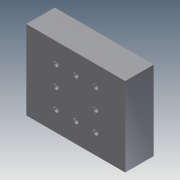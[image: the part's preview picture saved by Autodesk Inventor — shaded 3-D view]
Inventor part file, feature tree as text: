
AUTODESK INVENTOR PART (.ipt)
format: ipt  version: 2011 (Build 150239000, 239)  size: 123,904 bytes
history: native  units: in
note: dims shown in document units (in); Inventor stores cm internally (conversion verified against a paired STEP export)
features: extrude x5, sketch x5
ambient origin geometry x8: Origin, YZ Plane, XZ Plane, XY Plane, X Axis, Y Axis, Z Axis, Center Point
bodies: Solid1 (feature_tree)
feature tree (10):
  extrude  "Extrusion1"  Depth=1.1811in
  extrude  "Extrusion2"  Depth=0.315in
  extrude  "Extrusion3"  Depth=0.6299in
  extrude  "Extrusion4"  Depth=0.6299in
  extrude  "Extrusion5"  Depth=0.0787in TaperAngle=0.0deg
  sketch  "Sketch1"  dims[d0=1.5748in d1=1.1811in]
  sketch  "Sketch2"  dims[d2=0.0787in d3=0.0in d4=0.315in]
  sketch  "Sketch3"  dims[d5=0.315in d6=0.6299in]
  sketch  "Sketch4"  dims[d7=0.6299in d8=0.6299in]
  sketch  "Sketch5"  dims[d9=0.0787in d10=0.0787in d11=0.0in d12=0.0394in d13=0.0in d14=0.0394in d15=0.0in d16=0.375in d17=0.0in]
